# Revit family: DC_Rheem_PLM_ StorageTank_610430
name_source: partatom
category: Mechanical Equipment
revit_build: Autodesk Revit 2018 (Build: 20170223_1515(x64)
units: mm (PartAtom-declared; Revit-internal decimal feet)

## family parameters
Cut with Voids When Loaded = No
Host = Face
Part Type = Normal
Room Calculation Point = No
Round Connector Dimension = Use Radius
Shared = No

## types (1)
- DC_Rheem_PLM_ StorageTank_610430
    ColdWater&PrimaryFlowDiameter_ANZRS = 50 mm
    ColdWater&PrimaryFlowRadius_ANZRS = 25 mm  [stored 0.082021 ft]
    Default Elevation = 0 mm  [stored 0 ft]
    Description = Storage Tank- Indoor/Outdoor - 410L
    Diameter_ANZRS = 686 mm  [stored 2.25066 ft]
    Height_ANZRS = 1836 mm  [stored 6.02362 ft]
    HotWaterOutletDiameter_ANZRS = 50 mm
    HotWaterOutletRadius_ANZRS = 25 mm  [stored 0.082021 ft]
    Manufacturer = Rheem
    Material_ANZRS = Rheem - Joey Grey Steel
    Model = 610430
    PrimaryReturnConnectorDiameter_ANZRS = 50 mm
    PrimaryReturnConnectorRadius_ANZRS = 25 mm  [stored 0.082021 ft]
    Radius_ANZRS = 343 mm  [stored 1.12533 ft]
    T&PRValveDiameter_ANZRS = 20 mm  [stored 0.0656168 ft]
    T&PRValveRadius_ANZRS = 10 mm  [stored 0.0328084 ft]
    URL = http://www.rheem.com.au

note: [stored X ft] marks values corroborated as IEEE doubles in the binary element streams (Revit-internal decimal feet)

## geometry (parser evidence)
native form markers: Blend x6, Sweep x3
no freeform markers — native parametric forms only
